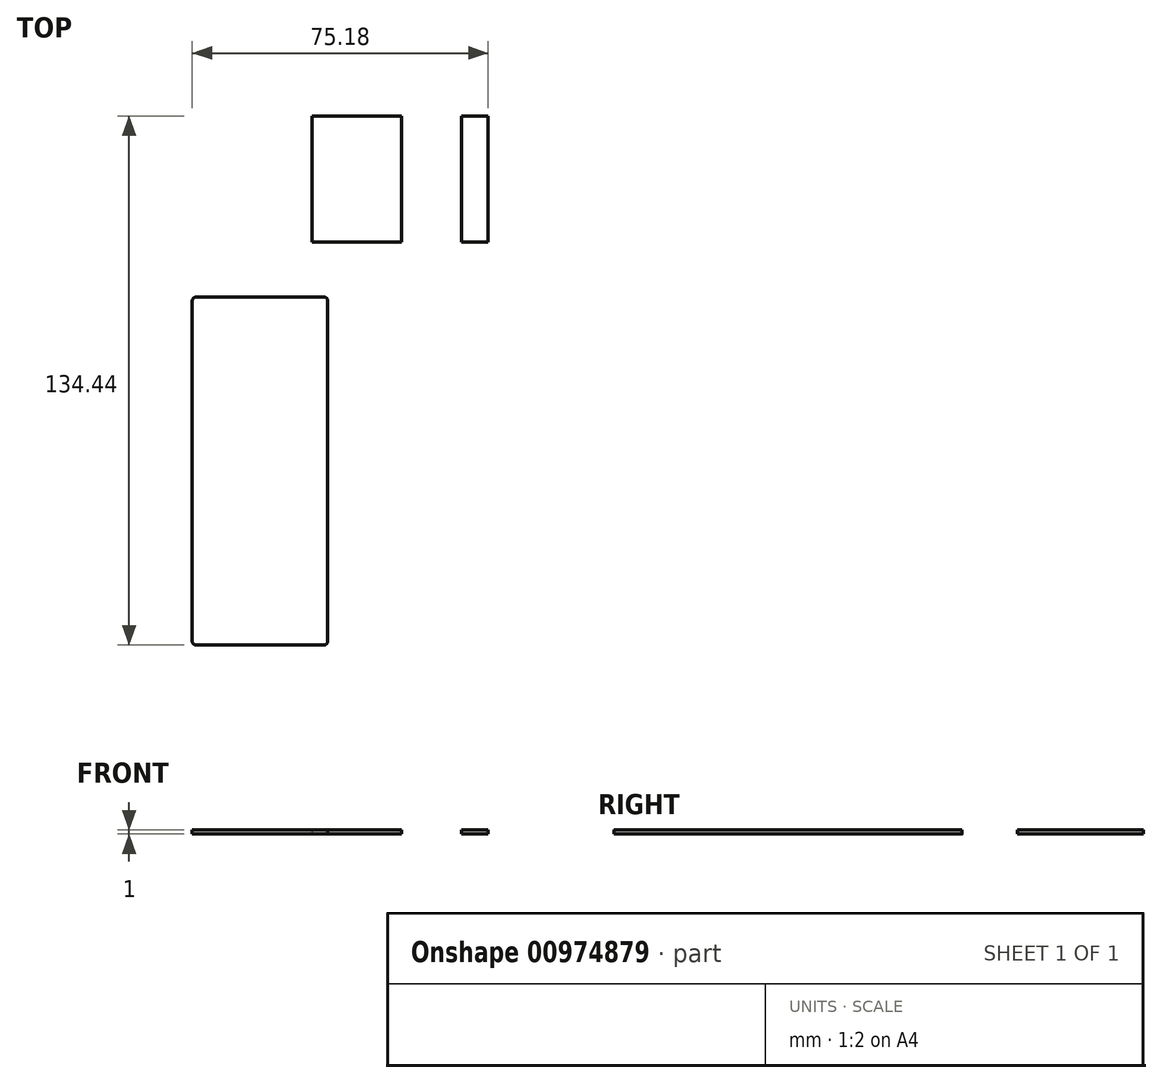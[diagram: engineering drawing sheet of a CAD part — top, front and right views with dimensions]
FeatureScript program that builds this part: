
annotation { "Feature Type Name" : "Feature", "Feature Type Description" : "" }
export const myFeature = defineFeature(function(context is Context, id is Id, definition is map)
    precondition{}
    {
        {
            var Q0;
            Q0=qCreatedBy(makeId("Top.planeOp"),FACE);
            var sketch = newSketch(context, id + "F0", { "sketchPlane" : qUnion([Q0])});
            skLineSegment(sketch, "E0.bottom", {"start": v(0, 0) * mm, "end": v(-22.7, 0) * mm});
            skLineSegment(sketch, "E0.top", {"start": v(0, 32) * mm, "end": v(-22.7, 32) * mm});
            skLineSegment(sketch, "E0.left", {"start": v(0, 0) * mm, "end": v(0, 32) * mm});
            skLineSegment(sketch, "E0.right", {"start": v(-22.7, 0) * mm, "end": v(-22.7, 32) * mm});
            skLineSegment(sketch, "E1.bottom", {"start": v(15.18, 0) * mm, "end": v(21.99, 0) * mm});
            skLineSegment(sketch, "E1.top", {"start": v(15.18, 32) * mm, "end": v(21.99, 32) * mm});
            skLineSegment(sketch, "E1.left", {"start": v(15.18, 0) * mm, "end": v(15.18, 32) * mm});
            skLineSegment(sketch, "E1.right", {"start": v(21.99, 0) * mm, "end": v(21.99, 32) * mm});
            skLineSegment(sketch, "E2.bottom", {"start": v(-52.19, -14.02) * mm, "end": v(-19.76, -14.02) * mm});
            skLineSegment(sketch, "E2.top", {"start": v(-52.19, -102.44) * mm, "end": v(-19.76, -102.44) * mm});
            skLineSegment(sketch, "E2.left", {"start": v(-53.19, -15.02) * mm, "end": v(-53.19, -101.44) * mm});
            skLineSegment(sketch, "E2.right", {"start": v(-18.76, -15.02) * mm, "end": v(-18.76, -101.44) * mm});
            skPoint(sketch, "E3.visualSharp", {"position": v(-53.19, -14.02) * mm});
            skArc(sketch, "E3.filletArc", {"start": v(-52.19, -14.02) * mm, "mid": v(-52.9, -14.31) * mm, "end": v(-53.19, -15.02) * mm});
            skPoint(sketch, "E4.visualSharp", {"position": v(-18.76, -14.02) * mm});
            skArc(sketch, "E4.filletArc", {"start": v(-18.76, -15.02) * mm, "mid": v(-19.05, -14.31) * mm, "end": v(-19.76, -14.02) * mm});
            skPoint(sketch, "E5.visualSharp", {"position": v(-53.19, -102.44) * mm});
            skArc(sketch, "E5.filletArc", {"start": v(-53.19, -101.44) * mm, "mid": v(-52.9, -102.14) * mm, "end": v(-52.19, -102.44) * mm});
            skPoint(sketch, "E6.visualSharp", {"position": v(-18.76, -102.44) * mm});
            skArc(sketch, "E6.filletArc", {"start": v(-19.76, -102.44) * mm, "mid": v(-19.05, -102.14) * mm, "end": v(-18.76, -101.44) * mm});
            skSolve(sketch);
        }
        {
            var Q0;
            Q0=makeQuery(id+"F0.imprint","IMPRINT",FACE,{"disambiguationData":[TD([[makeQuery(id+"F0.imprint","IMPRINT",EDGE,{"derivedFrom":sQuery(id+"F0.wireOp",EDGE,"E1.bottom")}),1.0]])]});
            var Q1;
            Q1=makeQuery(id+"F0.imprint","IMPRINT",FACE,{"disambiguationData":[TD([[makeQuery(id+"F0.imprint","IMPRINT",EDGE,{"derivedFrom":sQuery(id+"F0.wireOp",EDGE,"E2.bottom")}),-1.0]])]});
            var Q2;
            Q2=makeQuery(id+"F0.imprint","IMPRINT",FACE,{"disambiguationData":[TD([[makeQuery(id+"F0.imprint","IMPRINT",EDGE,{"derivedFrom":sQuery(id+"F0.wireOp",EDGE,"E0.bottom")}),-1.0]])]});
            extrude(context, id + "F1", {"entities" : qUnion([Q0, Q1, Q2]), "depth" : 1 * mm, "offsetDistance" : 25 * mm});
        }
    });
